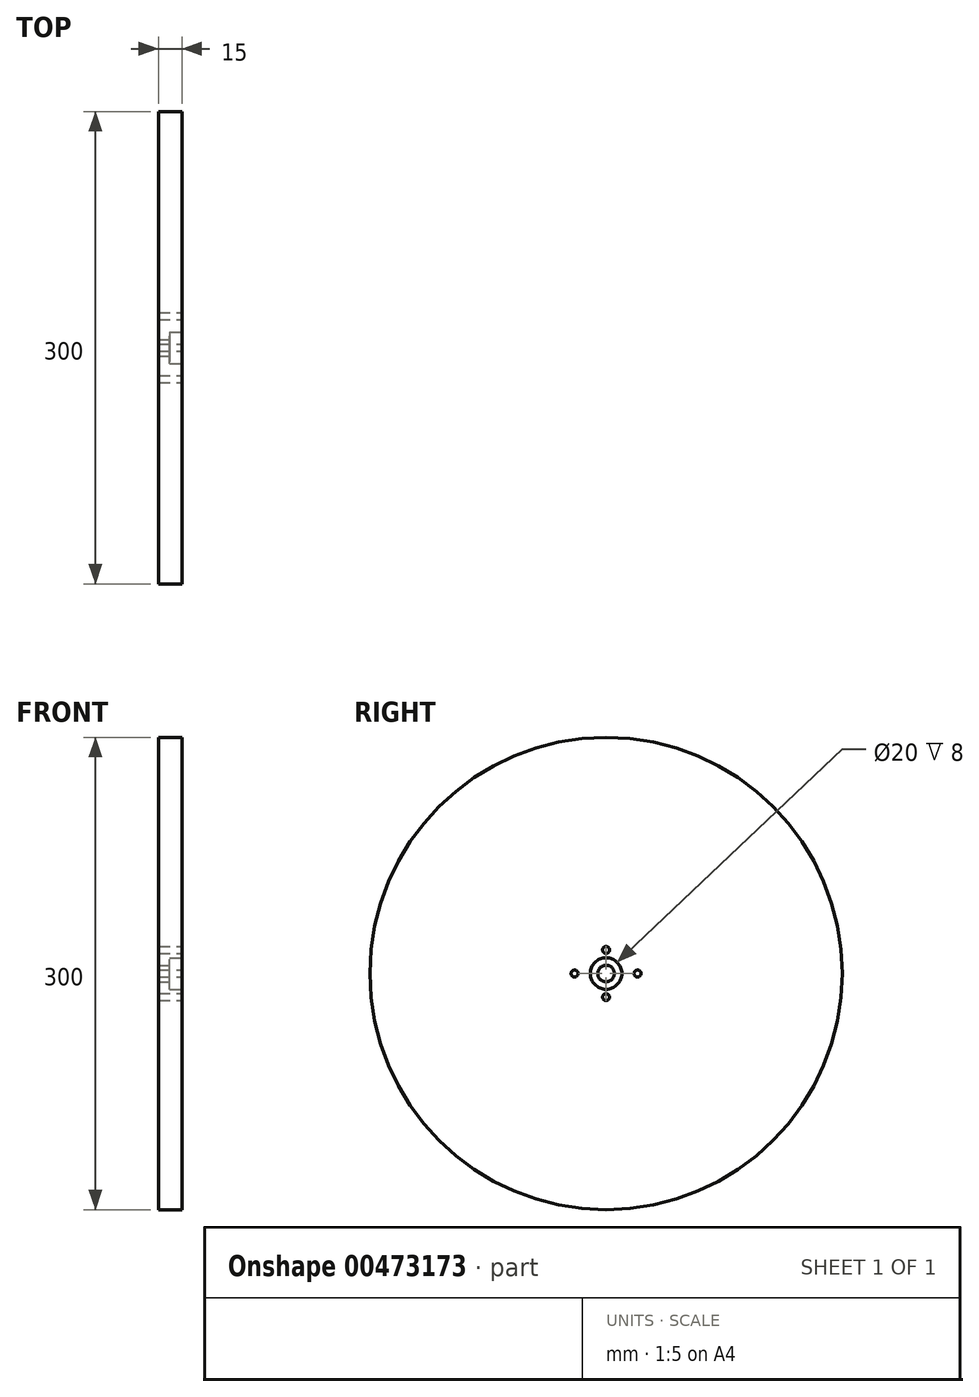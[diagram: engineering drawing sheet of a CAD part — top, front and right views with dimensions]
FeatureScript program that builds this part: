
annotation { "Feature Type Name" : "Feature", "Feature Type Description" : "" }
export const myFeature = defineFeature(function(context is Context, id is Id, definition is map)
    precondition{}
    {
        {
            assignVariable(context, id + "F0", {"name" : "Epaisseur_Disque", "anyValue" : 15});
        }
        {
            assignVariable(context, id + "F1", {"name" : "Profondeur_Roulement", "anyValue" : 8});
        }
        {
            var Q0;
            Q0=qCreatedBy(makeId("Right.planeOp"),FACE);
            var sketch = newSketch(context, id + "F2", { "sketchPlane" : qUnion([Q0])});
            skCircle(sketch, "E0", {"center": v(0, 0) * mm, "radius": 150 * mm});
            skCircle(sketch, "E1", {"center": v(0, 0) * mm, "radius": 5.25 * mm});
            skCircle(sketch, "E2", {"center": v(20, 0) * mm, "radius": 2.2 * mm});
            skCircle(sketch, "E3", {"center": v(0, 15) * mm, "radius": 2.2 * mm});
            skCircle(sketch, "E4.MirrorC", {"center": v(0, -15) * mm, "radius": 2.2 * mm});
            skCircle(sketch, "E5.MirrorC", {"center": v(-20, 0) * mm, "radius": 2.2 * mm});
            skCircle(sketch, "E6", {"center": v(0, 0) * mm, "radius": 10 * mm});
            skSolve(sketch);
        }
        {
            var Q0;
            Q0=makeQuery(id+"F2.imprint","IMPRINT",FACE,{"disambiguationData":[TD([[makeQuery(id+"F2.imprint","IMPRINT",EDGE,{"derivedFrom":sQuery(id+"F2.wireOp",EDGE,"E0")}),1.0]])]});
            var Q1;
            Q1=makeQuery(id+"F2.imprint","IMPRINT",FACE,{"disambiguationData":[TD([[makeQuery(id+"F2.imprint","IMPRINT",EDGE,{"derivedFrom":sQuery(id+"F2.wireOp",EDGE,"E1")}),-1.0]])]});
            extrude(context, id + "F3", {"entities" : qUnion([Q0, Q1]), "oppositeDirection" : true, "depth" : getVariable(context, 'Epaisseur_Disque') * mm, "offsetDistance" : 25 * mm});
        }
        {
            var Q0;
            Q0=makeQuery(id+"F2.imprint","IMPRINT",FACE,{"disambiguationData":[TD([[makeQuery(id+"F2.imprint","IMPRINT",EDGE,{"derivedFrom":sQuery(id+"F2.wireOp",EDGE,"E1")}),-1.0]])]});
            extrude(context, id + "F4", {"entities" : qUnion([Q0]), "operationType" : NewBodyOperationType.REMOVE, "oppositeDirection" : true, "depth" : getVariable(context, 'Profondeur_Roulement') * mm, "offsetDistance" : 25 * mm});
        }
    });
